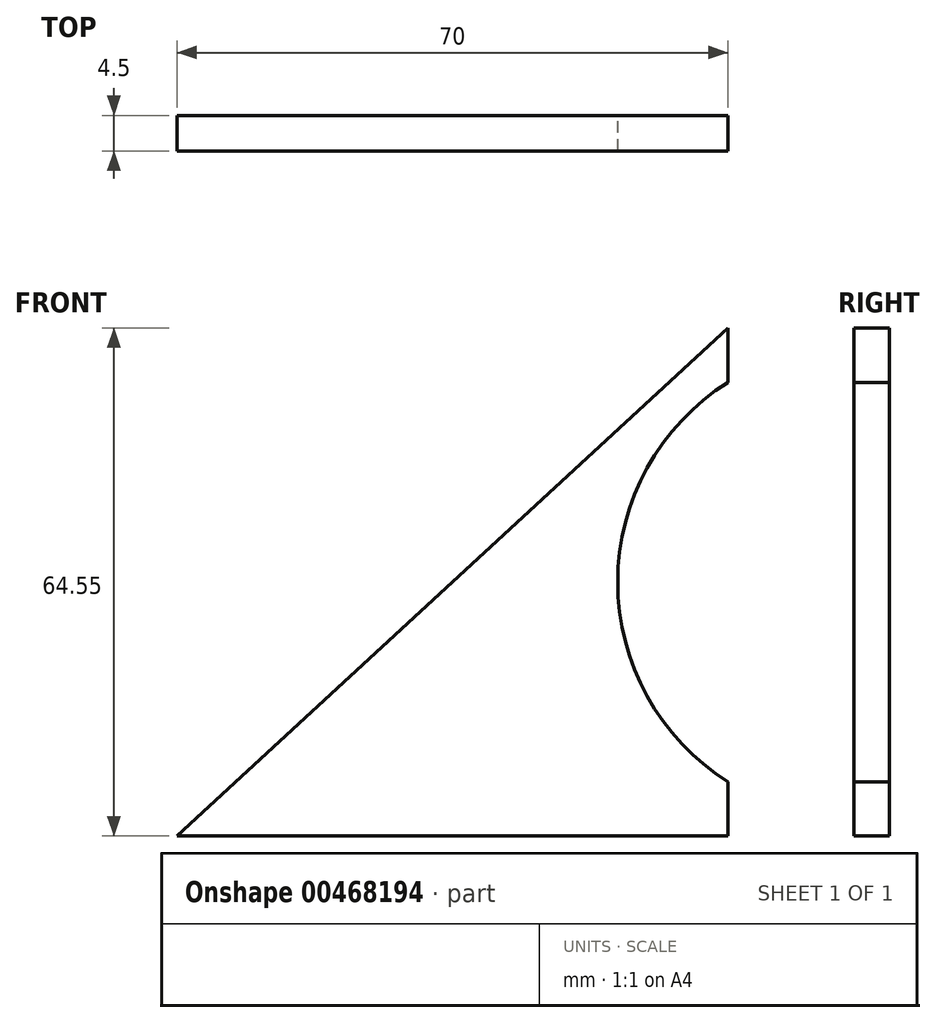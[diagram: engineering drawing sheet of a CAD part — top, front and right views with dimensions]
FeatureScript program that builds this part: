
annotation { "Feature Type Name" : "Feature", "Feature Type Description" : "" }
export const myFeature = defineFeature(function(context is Context, id is Id, definition is map)
    precondition{}
    {
        {
            var Q0;
            Q0=qCreatedBy(makeId("Front.planeOp"),FACE);
            var sketch = newSketch(context, id + "F0", { "sketchPlane" : qUnion([Q0])});
            skLineSegment(sketch, "E0", {"start": v(0, 0) * mm, "end": v(70, 0) * mm});
            skPoint(sketch, "E1", {"position": v(70, 64.55) * mm});
            skLineSegment(sketch, "E2", {"start": v(0, 0) * mm, "end": v(70, 64.55) * mm});
            skLineSegment(sketch, "E3", {"start": v(70, 0) * mm, "end": v(70, 64.55) * mm});
            skPoint(sketch, "E4", {"position": v(70, 32.27) * mm});
            skLineSegment(sketch, "E5", {"start": v(70, 32.27) * mm, "end": v(86, 32.27) * mm});
            skPoint(sketch, "E6", {"position": v(86, 32.27) * mm});
            skCircle(sketch, "E7", {"center": v(86, 32.27) * mm, "radius": 30 * mm});
            skPoint(sketch, "E8", {"position": v(65, 0) * mm});
            skLineSegment(sketch, "E9.bottom", {"start": v(65, 0) * mm, "end": v(36, 0) * mm});
            skLineSegment(sketch, "E9.top", {"start": v(65, -5) * mm, "end": v(36, -5) * mm});
            skLineSegment(sketch, "E9.left", {"start": v(65, 0) * mm, "end": v(65, -5) * mm});
            skLineSegment(sketch, "E9.right", {"start": v(36, 0) * mm, "end": v(36, -5) * mm});
            skSolve(sketch);
        }
        {
            var Q0;
            {var subQ5=sQuery(id+"F0.wireOp",EDGE,"E2");Q0=makeQuery(id+"F0.imprint","IMPRINT",FACE,{"disambiguationData":[TD([[makeQuery(id+"F0.imprint","IMPRINT",EDGE,{"derivedFrom":subQ5}),-1.0]])]});}
            var Q1;
            Q1=makeQuery(id+"F0.imprint","IMPRINT",FACE,{"disambiguationData":[TD([[makeQuery(id+"F0.imprint","IMPRINT",EDGE,{"derivedFrom":sQuery(id+"F0.wireOp",EDGE,"E9.bottom")}),1.0]])]});
            extrude(context, id + "F1", {"entities" : qUnion([Q0, Q1]), "depth" : 4.5 * mm});
        }
    });
